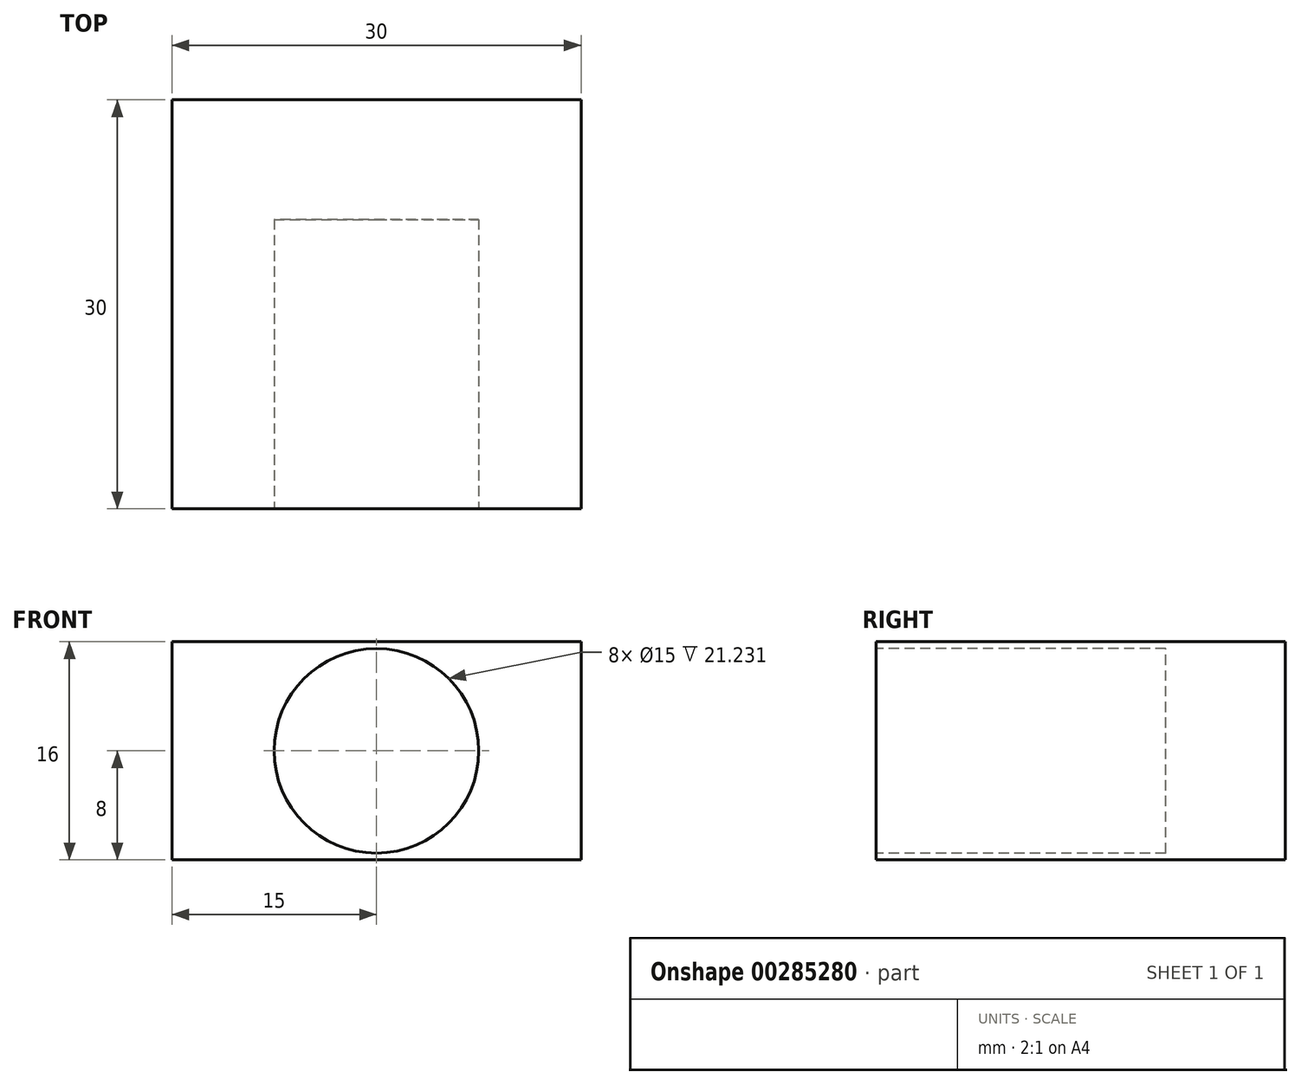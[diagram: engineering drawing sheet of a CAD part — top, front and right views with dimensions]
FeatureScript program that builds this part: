
annotation { "Feature Type Name" : "Feature", "Feature Type Description" : "" }
export const myFeature = defineFeature(function(context is Context, id is Id, definition is map)
    precondition{}
    {
        {
            var Q0;
            Q0=qCreatedBy(makeId("Front.planeOp"),FACE);
            var sketch = newSketch(context, id + "F0", { "sketchPlane" : qUnion([Q0])});
            skLineSegment(sketch, "E0.bottom", {"start": v(0, 0) * mm, "end": v(30, 0) * mm});
            skLineSegment(sketch, "E0.top", {"start": v(0, 16) * mm, "end": v(30, 16) * mm});
            skLineSegment(sketch, "E0.left", {"start": v(0, 0) * mm, "end": v(0, 16) * mm});
            skLineSegment(sketch, "E0.right", {"start": v(30, 0) * mm, "end": v(30, 16) * mm});
            skSolve(sketch);
        }
        {
            var Q0;
            Q0=makeQuery(id+"F0.imprint","IMPRINT",FACE,{"disambiguationData":[TD([[makeQuery(id+"F0.imprint","IMPRINT",EDGE,{"derivedFrom":sQuery(id+"F0.wireOp",EDGE,"E0.bottom")}),1.0]])]});
            extrude(context, id + "F1", {"entities" : qUnion([Q0]), "depth" : 30 * mm});
        }
        {
            var Q0;
            Q0=makeQuery(id+"F1.opExtrude","CAP_FACE",FACE,{"disambiguationData":[OSD([sQuery(id+"F0.wireOp",EDGE,"E0.bottom"),sQuery(id+"F0.wireOp",EDGE,"E0.top"),sQuery(id+"F0.wireOp",EDGE,"E0.left"),sQuery(id+"F0.wireOp",EDGE,"E0.right")])],"isStart":false});
            var sketch = newSketch(context, id + "F2", { "sketchPlane" : qUnion([Q0])});
            skCircle(sketch, "E1", {"center": v(15, 8) * mm, "radius": 7.5 * mm});
            skPoint(sketch, "E1.centerSnap0", {"position": v(15, 0) * mm});
            skPoint(sketch, "E1.centerSnap1", {"position": v(0, 8) * mm});
            skSolve(sketch);
        }
        {
            var Q0;
            Q0=makeQuery(id+"F2.imprint","IMPRINT",FACE,{"disambiguationData":[TD([[makeQuery(id+"F2.imprint","IMPRINT",EDGE,{"derivedFrom":sQuery(id+"F2.wireOp",EDGE,"E1")}),1.0]])]});
            extrude(context, id + "F3", {"entities" : qUnion([Q0]), "operationType" : NewBodyOperationType.REMOVE, "oppositeDirection" : true, "depth" : 21.23 * mm});
        }
    });
